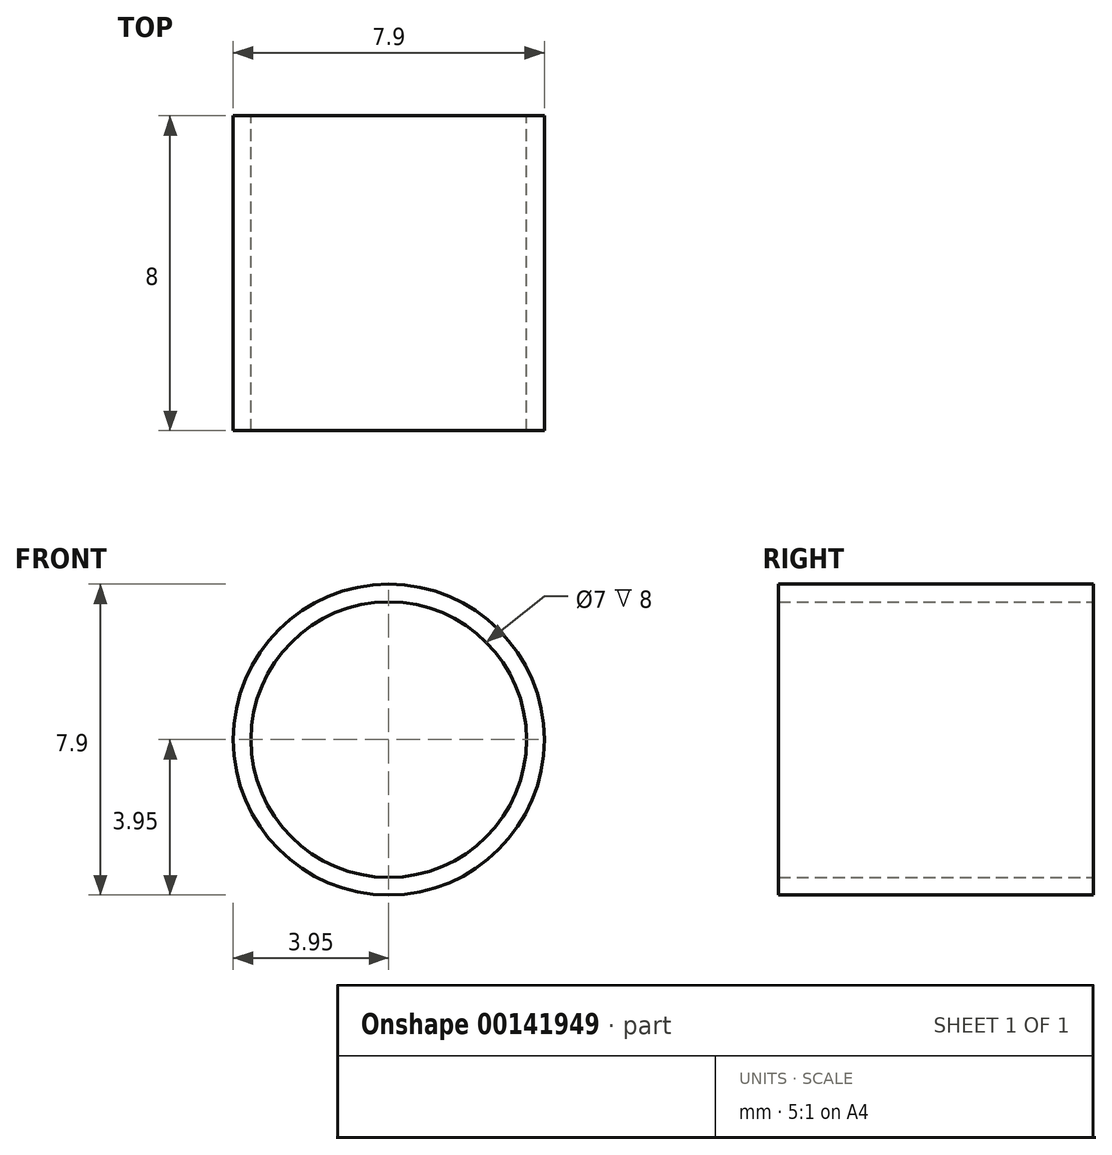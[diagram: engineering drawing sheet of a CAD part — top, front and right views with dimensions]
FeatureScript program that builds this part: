
annotation { "Feature Type Name" : "Feature", "Feature Type Description" : "" }
export const myFeature = defineFeature(function(context is Context, id is Id, definition is map)
    precondition{}
    {
        {
            var Q0;
            Q0=qCreatedBy(makeId("Front.planeOp"),FACE);
            var sketch = newSketch(context, id + "F0", { "sketchPlane" : qUnion([Q0])});
            skCircle(sketch, "E0", {"center": v(0, 0) * mm, "radius": 3.5 * mm});
            skCircle(sketch, "E1", {"center": v(0, 0) * mm, "radius": 3.95 * mm});
            skSolve(sketch);
        }
        {
            var Q0;
            Q0=makeQuery(id+"F0.imprint","IMPRINT",FACE,{"disambiguationData":[TD([[makeQuery(id+"F0.imprint","IMPRINT",EDGE,{"derivedFrom":sQuery(id+"F0.wireOp",EDGE,"E0")}),-1.0]])]});
            extrude(context, id + "F1", {"entities" : qUnion([Q0]), "depth" : 8 * mm, "offsetDistance" : 25 * mm});
        }
    });
